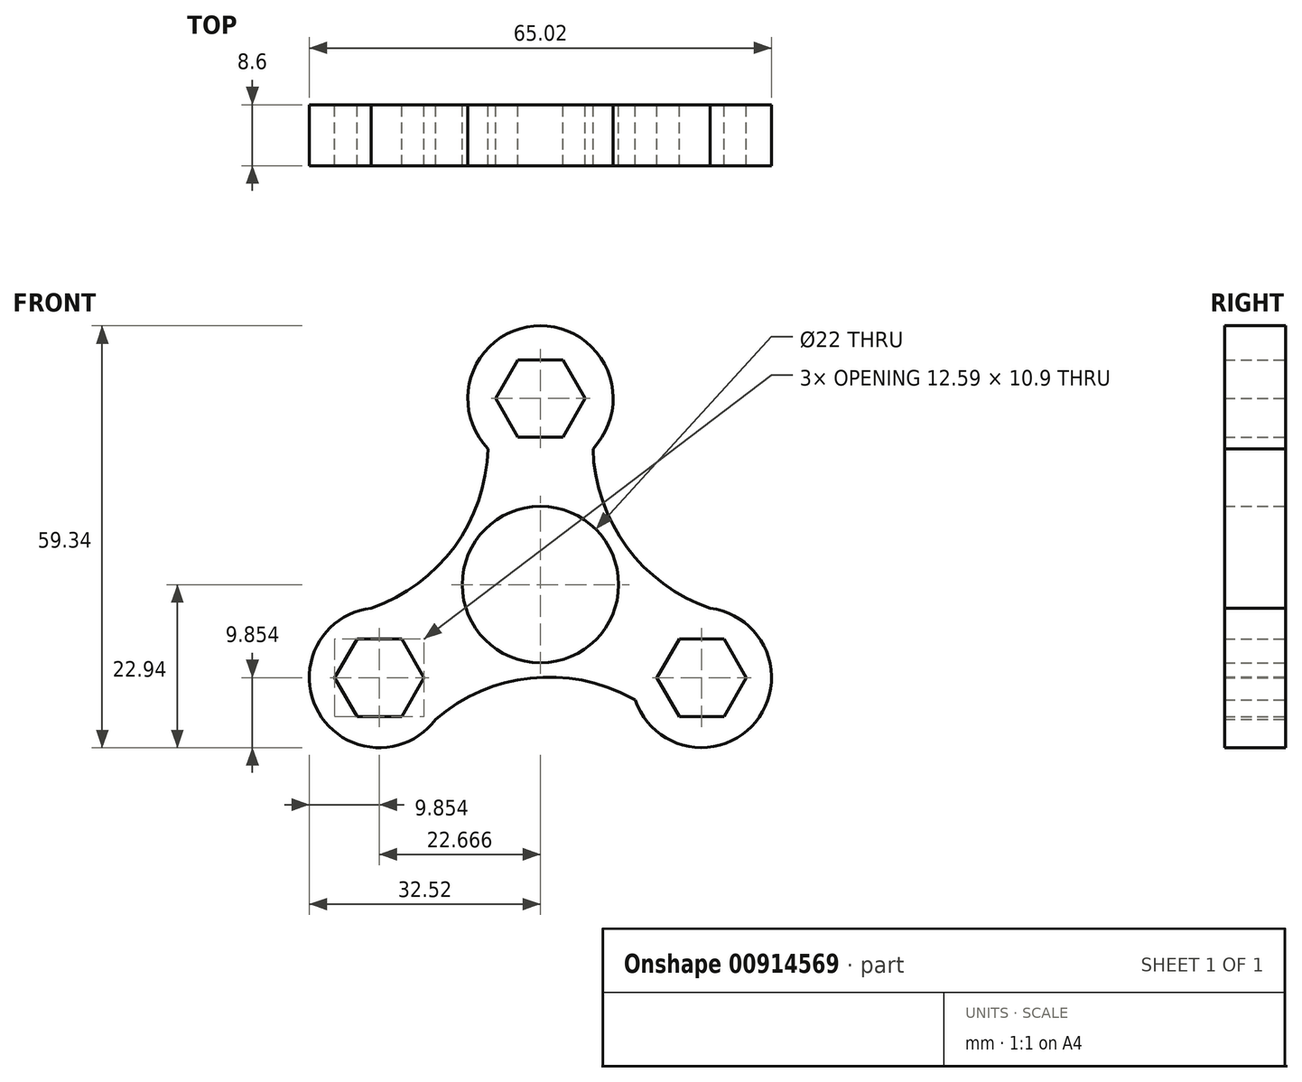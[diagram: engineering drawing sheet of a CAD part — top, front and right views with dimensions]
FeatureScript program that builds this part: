
annotation { "Feature Type Name" : "Feature", "Feature Type Description" : "" }
export const myFeature = defineFeature(function(context is Context, id is Id, definition is map)
    precondition{}
    {
        {
            var Q0;
            Q0=qCreatedBy(makeId("Front.planeOp"),FACE);
            var sketch = newSketch(context, id + "F0", { "sketchPlane" : qUnion([Q0])});
            skArc(sketch, "E0", {"start": v(-23.8, -3.3) * mm, "mid": v(-31.2, -18.01) * mm, "end": v(-14.76, -18.97) * mm});
            skArc(sketch, "E1", {"start": v(13.35, -16.23) * mm, "mid": v(30.28, -19.31) * mm, "end": v(23.9, -3.33) * mm});
            skArc(sketch, "E2", {"start": v(7.4, 19.11) * mm, "mid": v(0, 36.4) * mm, "end": v(-7.4, 19.11) * mm});
            skArc(sketch, "E3", {"start": v(7.4, 19.11) * mm, "mid": v(12.12, 5.3) * mm, "end": v(23.9, -3.33) * mm});
            skCircle(sketch, "E4.cCircle", {"center": v(-22.67, -13.09) * mm, "radius": 5.45 * mm, "construction": true});
            skLineSegment(sketch, "E4.0", {"start": v(-25.81, -18.54) * mm, "end": v(-28.96, -13.09) * mm});
            skLineSegment(sketch, "E4.1", {"start": v(-28.96, -13.09) * mm, "end": v(-25.81, -7.64) * mm});
            skLineSegment(sketch, "E4.2", {"start": v(-25.81, -7.64) * mm, "end": v(-19.52, -7.64) * mm});
            skLineSegment(sketch, "E4.3", {"start": v(-19.52, -7.64) * mm, "end": v(-16.37, -13.09) * mm});
            skLineSegment(sketch, "E4.4", {"start": v(-16.37, -13.09) * mm, "end": v(-19.52, -18.54) * mm});
            skLineSegment(sketch, "E4.5", {"start": v(-19.52, -18.54) * mm, "end": v(-25.81, -18.54) * mm});
            skPoint(sketch, "E4.0.midPoint", {"position": v(-27.39, -15.81) * mm});
            skCircle(sketch, "E5.cCircle", {"center": v(22.67, -13.09) * mm, "radius": 5.45 * mm, "construction": true});
            skLineSegment(sketch, "E5.0", {"start": v(19.52, -18.54) * mm, "end": v(16.37, -13.09) * mm});
            skLineSegment(sketch, "E5.1", {"start": v(16.37, -13.09) * mm, "end": v(19.52, -7.64) * mm});
            skLineSegment(sketch, "E5.2", {"start": v(19.52, -7.64) * mm, "end": v(25.81, -7.64) * mm});
            skLineSegment(sketch, "E5.3", {"start": v(25.81, -7.64) * mm, "end": v(28.96, -13.09) * mm});
            skLineSegment(sketch, "E5.4", {"start": v(28.96, -13.09) * mm, "end": v(25.81, -18.54) * mm});
            skLineSegment(sketch, "E5.5", {"start": v(25.81, -18.54) * mm, "end": v(19.52, -18.54) * mm});
            skPoint(sketch, "E5.0.midPoint", {"position": v(17.95, -15.81) * mm});
            skArc(sketch, "E6.cCircle", {"start": v(4.72, 23.45) * mm, "mid": v(-2.72, 30.9) * mm, "end": v(0, 20.72) * mm, "construction": true});
            skLineSegment(sketch, "E6.0", {"start": v(3.15, 20.72) * mm, "end": v(-3.15, 20.72) * mm});
            skLineSegment(sketch, "E6.1", {"start": v(-3.15, 20.72) * mm, "end": v(-6.3, 26.17) * mm});
            skLineSegment(sketch, "E6.2", {"start": v(-6.3, 26.17) * mm, "end": v(-3.15, 31.62) * mm});
            skLineSegment(sketch, "E6.3", {"start": v(-3.15, 31.62) * mm, "end": v(3.15, 31.62) * mm});
            skLineSegment(sketch, "E6.4", {"start": v(3.15, 31.62) * mm, "end": v(6.3, 26.17) * mm});
            skLineSegment(sketch, "E6.5", {"start": v(6.3, 26.17) * mm, "end": v(3.15, 20.72) * mm});
            skCircle(sketch, "E7", {"center": v(0, 0) * mm, "radius": 11 * mm});
            skArc(sketch, "E8.MirrorCS", {"start": v(-7.4, 19.11) * mm, "mid": v(-12.12, 5.3) * mm, "end": v(-23.9, -3.33) * mm});
            skArc(sketch, "E9.MirrorCS", {"start": v(12.85, -15.96) * mm, "mid": v(-1.47, -13.15) * mm, "end": v(-14.83, -19.03) * mm});
            skLineSegment(sketch, "E10", {"start": v(12.85, -15.96) * mm, "end": v(13.35, -16.23) * mm});
            skSolve(sketch);
        }
        {
            var Q0;
            Q0 = qSketchRegion(id + "F0", true);
            extrude(context, id + "F1", {"entities" : qUnion([Q0]), "endBound" : BoundingType.SYMMETRIC, "depth" : 8.6 * mm, "offsetDistance" : 25 * mm});
        }
    });
